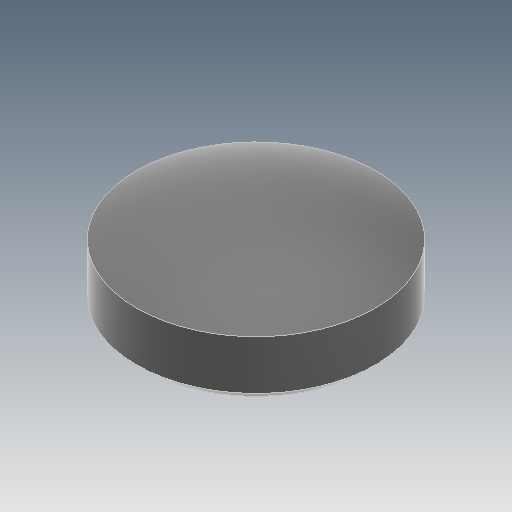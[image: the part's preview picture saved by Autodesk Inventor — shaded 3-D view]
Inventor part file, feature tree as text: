
AUTODESK INVENTOR PART (.ipt)
format: ipt  version: 2025 (Build 290162000, 162)  size: 332,288 bytes
history: native  units: mm
features: revolve x1, thread x1, sketch x1
ambient origin geometry x8: Origin, YZ Plane, XZ Plane, XY Plane, X Axis, Y Axis, Z Axis, Center Point
bodies: 实体1 (feature_tree)
feature tree (3):
  revolve  "旋转1"  Angle=45.0deg
  thread  "螺纹1"  [1 undecoded]
  sketch  "草图2"  dims[d1=48.0mm d2=12.0mm d3=5.0mm d4=22.0mm d0=45.0deg d5=2.0mm d6=27.5mm d7=20.0mm d8=60.0mm d9=360.0deg d10=1.0mm d11=1.0mm d12=2.0mm d13=2.0mm d14=7.0mm d15=18.45mm d16=24.0mm d17=20.0mm d18=0.0mm]
note: 1 required parameter value undecoded (feature->parameter linkage not recoverable at this tier; creation-order binding heuristic only, values carry confidence <= 0.55)
